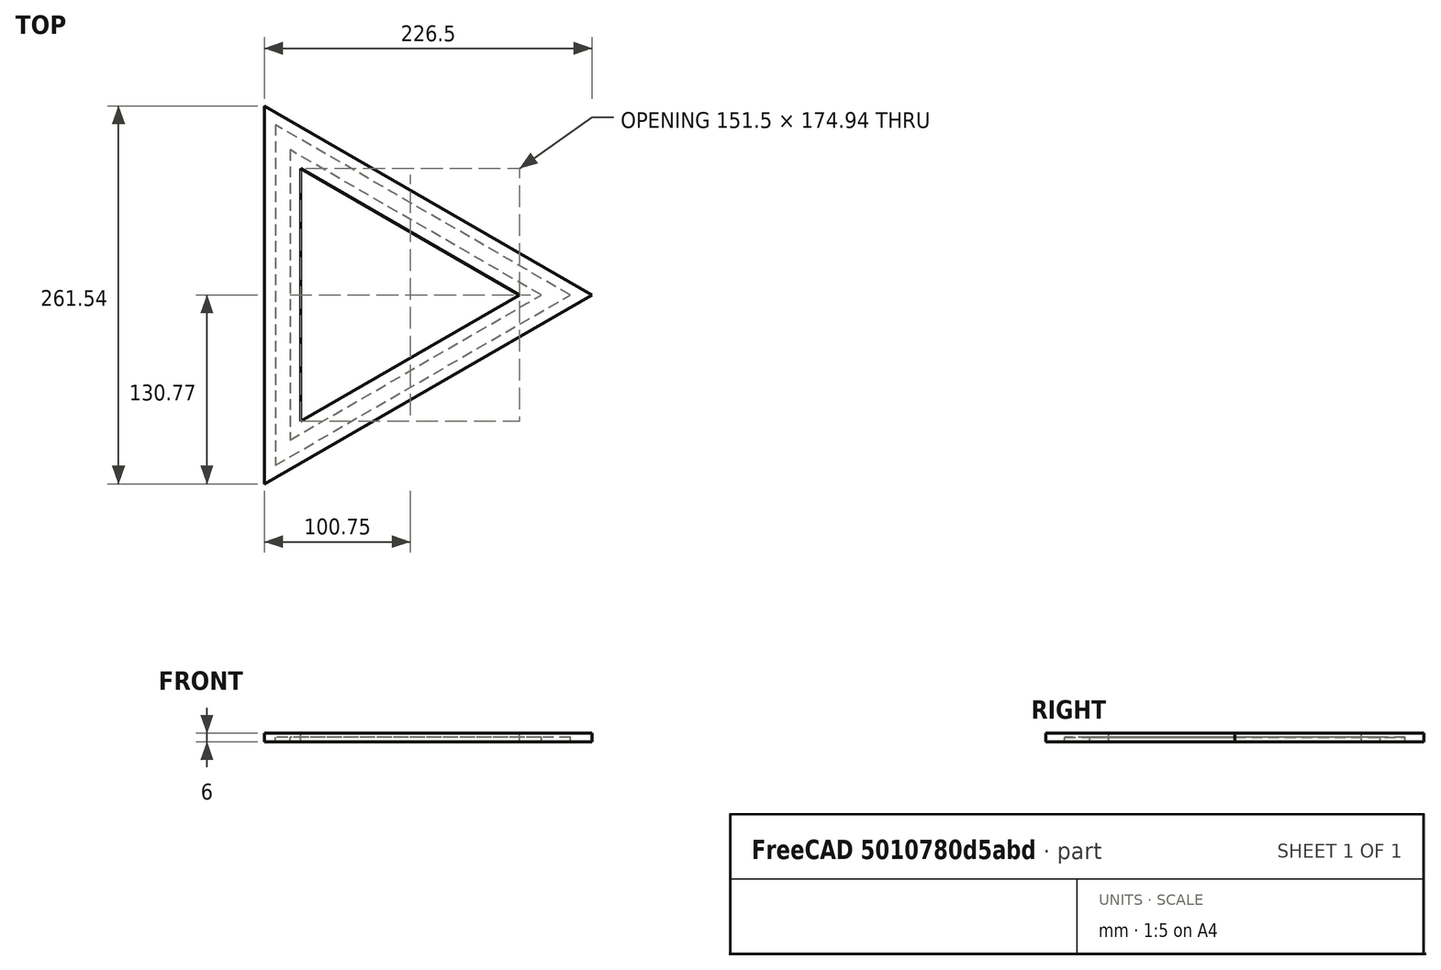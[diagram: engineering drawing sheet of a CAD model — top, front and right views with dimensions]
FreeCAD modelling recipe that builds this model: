
FCSTD DOCUMENT  (FreeCAD 0.15R4671 (Git))
Label: Triangle-Light-36-grooves-thin
License: All rights reserved
LicenseURL: http://en.wikipedia.org/wiki/All_rights_reserved
objects: App::MeasureDistance×6, Part::Prism×4, Part::Cut×3
note: 7 computed .brp shape members not serialized (recipe doc carries the construction recipe); baked Part::Feature solids carry a one-line shape summary decoded from their .brp

FEATURE [Part::Prism] Prism
  Circumradius = 136
  Height = 3
  Polygon = 3
FEATURE [Part::Prism] Prism001
  Circumradius = 116
  Height = 3
  Polygon = 3
FEATURE [Part::Cut] Cut
  Base = -> Prism
  Tool = -> Prism001
FEATURE [Part::Prism] Prism002
  Circumradius = 151
  Height = 6
  Polygon = 3
FEATURE [Part::Prism] Prism003
  Circumradius = 101
  Height = 15
  Polygon = 3
FEATURE [Part::Cut] Cut001
  Base = -> Prism002
  Tool = -> Cut
FEATURE [Part::Cut] Cut002
  Base = -> Cut001
  Tool = -> Prism003
FEATURE [App::MeasureDistance] Distance  label="Distance: 200.918"
  Distance = 200.918
  P1 = (-58,100.459,0)
  P2 = (116,0,0)
FEATURE [App::MeasureDistance] Distance001  label="Distance: 235.559"
  Distance = 235.559
  P1 = (-68,117.779,0)
  P2 = (136,0,0)
FEATURE [App::MeasureDistance] Distance002  label="Distance: 261.540"
  Distance = 261.54
  P1 = (-75.5,130.77,0)
  P2 = (151,0,0)
FEATURE [App::MeasureDistance] Distance003  label="Distance: 174.937"
  Distance = 174.937
  P1 = (-50.5,87.4686,0)
  P2 = (101,0,0)
FEATURE [App::MeasureDistance] Distance005  label="Distance: 7.530"
  Distance = 7.53007
  P1 = (38.3562,65.0349,0)
  P2 = (34.0239,58.8759,0)
FEATURE [App::MeasureDistance] Distance006  label="Distance: 10.351"
  Distance = 10.3512
  P1 = (-68,-2.93268,0)
  P2 = (-58,-0.259196,0)
